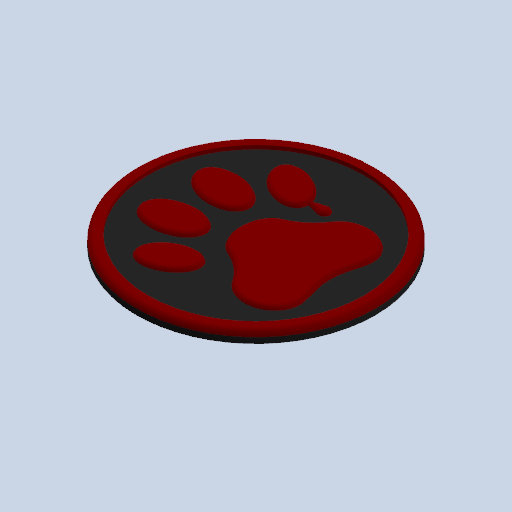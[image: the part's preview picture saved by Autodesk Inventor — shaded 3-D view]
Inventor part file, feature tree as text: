
AUTODESK INVENTOR PART (.ipt)
format: ipt  version: 2022 (Build 260153000, 153)  size: 405,504 bytes
history: native  units: mm
features: extrude x6, sketch x6, reference x6, other x5, fillet x4, projected_geometry x2
ambient origin geometry x8: Origin, YZ Plane, XZ Plane, XY Plane, X Axis, Y Axis, Z Axis, Center Point
bodies: Body1 (feature_tree)
feature tree (29):
  other  "Твердое тело1"
  extrude  "Выдавливание1"  Depth=64.0mm
  extrude  "Выдавливание2"  Depth=1.0mm TaperAngle=0.0deg
  fillet  "Сопряжение2"  Radius=62.0mm
  fillet  "Сопряжение3"  Radius=2.0mm
  extrude  "Выдавливание4"  Depth=15.0mm
  extrude  "Выдавливание9"  Depth=1.2mm
  extrude  "Выдавливание10"  Depth=0.6mm TaperAngle=0.0deg
  extrude  "Выдавливание11"  Depth=0.31mm
  fillet  "Сопряжение7"  Radius=6.7mm
  fillet  "Сопряжение8"  Radius=1.0mm
  sketch  "Эскиз1"
  sketch  "Эскиз2"
  sketch  "Эскиз4"
  reference  "Ссылка1"
  sketch  "Эскиз14"
  reference  "Ссылка2"
  sketch  "Эскиз15"
  reference  "Ссылка3"
  reference  "Ссылка4"
  reference  "Ссылка5"
  reference  "Ссылка6"
  sketch  "Эскиз16"
  projected_geometry  "Спроецированная петля7"
  projected_geometry  "Спроецированная петля8"
  other  "<userpath>\Documents\Git\MZCAT_2024\MZCAT_2.iam"
  other  "MZCAT_2.iam"
  other  "bearing 37x25x7:2"
  other  "wheel_fixator:1"
